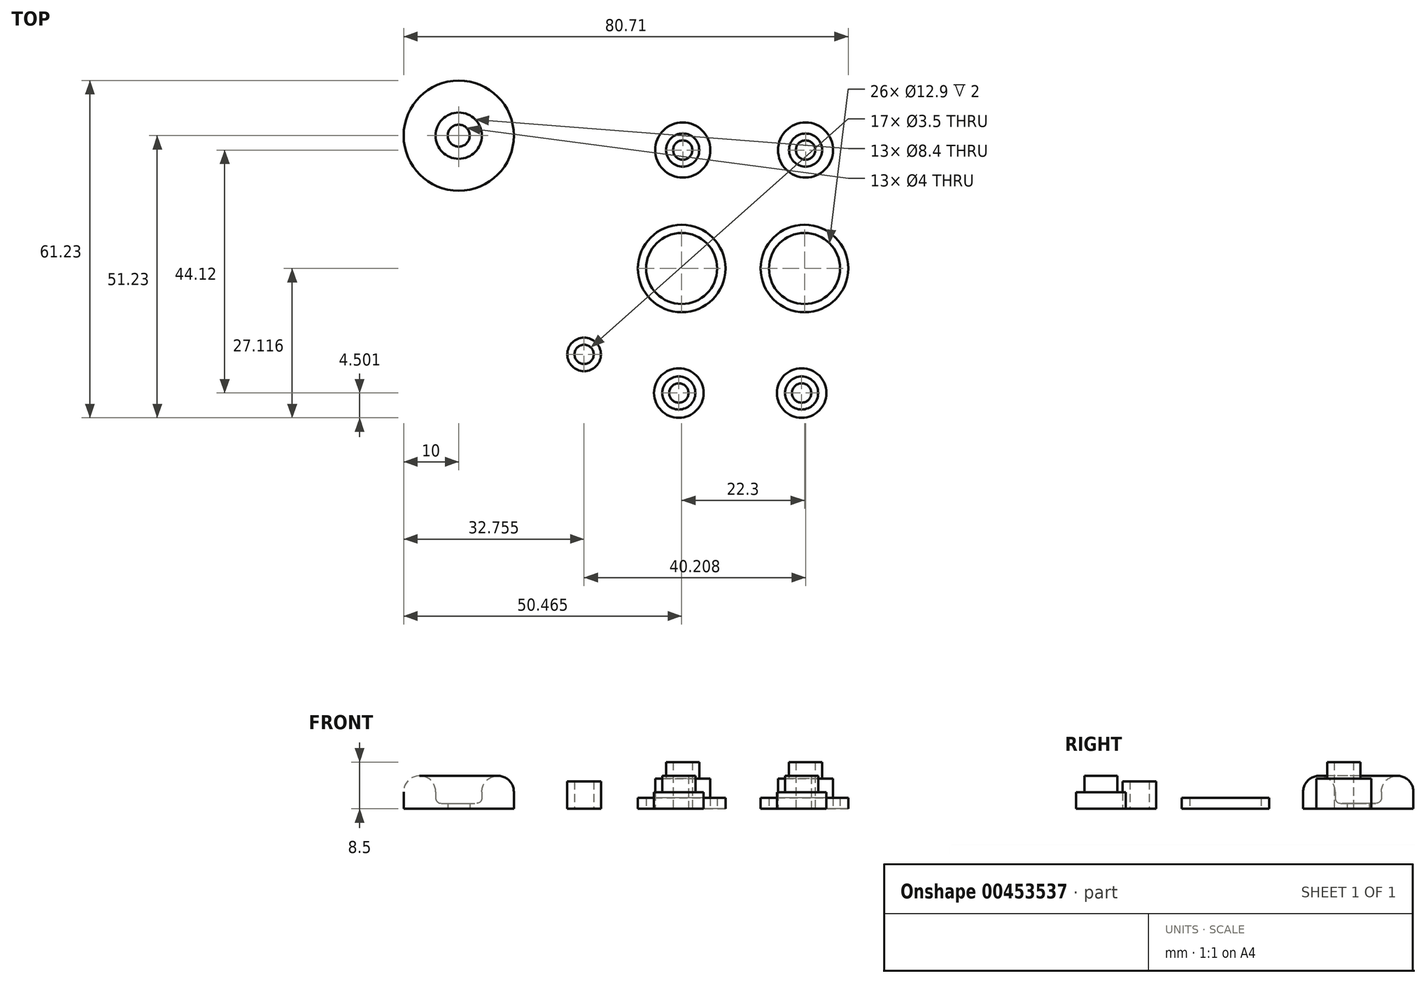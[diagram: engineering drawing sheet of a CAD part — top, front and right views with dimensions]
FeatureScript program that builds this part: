
annotation { "Feature Type Name" : "Feature", "Feature Type Description" : "" }
export const myFeature = defineFeature(function(context is Context, id is Id, definition is map)
    precondition{}
    {
        {
            var Q0;
            Q0=qCreatedBy(makeId("Front.planeOp"),FACE);
            var sketch = newSketch(context, id + "F0", { "sketchPlane" : qUnion([Q0])});
            skLineSegment(sketch, "E0.bottom", {"start": v(2, 0) * mm, "end": v(10, 0) * mm});
            skLineSegment(sketch, "E0.top", {"start": v(2, 1) * mm, "end": v(10, 1) * mm});
            skLineSegment(sketch, "E0.left", {"start": v(2, 0) * mm, "end": v(2, 1) * mm});
            skLineSegment(sketch, "E0.right", {"start": v(10, 0) * mm, "end": v(10, 1) * mm});
            skLineSegment(sketch, "E1", {"start": v(10, 1) * mm, "end": v(10, 3.1) * mm});
            skLineSegment(sketch, "E2", {"start": v(4.2, 1) * mm, "end": v(4.2, 3.1) * mm});
            skArc(sketch, "E3", {"start": v(10, 3.1) * mm, "mid": v(7.1, 6) * mm, "end": v(4.2, 3.1) * mm});
            skLineSegment(sketch, "E4", {"start": v(0, 0) * mm, "end": v(0, 11.31) * mm, "construction": true});
            skLineSegment(sketch, "E5", {"start": v(2.94, 6) * mm, "end": v(12.96, 6) * mm, "construction": true});
            skLineSegment(sketch, "E6", {"start": v(4.2, 3.1) * mm, "end": v(10, 3.1) * mm, "construction": true});
            skSolve(sketch);
        }
        {
            var Q0;
            Q0 = qSketchRegion(id + "F0", true);
            var Q1;
            Q1=sQuery(id+"F0.wireOp",EDGE,"E4");
            revolve(context, id + "F1", {"entities" : qUnion([Q0]), "axis" : qUnion([Q1]), "revolveType" : RevolveType.FULL});
        }
        {
            var Q0;
            Q0=makeQuery(id+"F1.opRevolve","SWEPT_EDGE",EDGE,{"disambiguationData":[OSD([sQuery(id+"F0.wireOp",EDGE,"E0.top"),sQuery(id+"F0.wireOp",EDGE,"E2")])]});
            fillet(context, id + "F2", {"entities" : qUnion([Q0]), "radius" : 1 * mm, "tangentPropagation" : true, "allowEdgeOverflow" : false});
        }
        {
            var Q0;
            Q0=qCreatedBy(makeId("Top.planeOp"),FACE);
            var sketch = newSketch(context, id + "F3", { "sketchPlane" : qUnion([Q0])});
            skCircle(sketch, "E7", {"center": v(22.75, -39.71) * mm, "radius": 1.75 * mm});
            skCircle(sketch, "E8", {"center": v(22.75, -39.71) * mm, "radius": 3.05 * mm});
            skSolve(sketch);
        }
        {
            var Q0;
            Q0 = qSketchRegion(id + "F3", true);
            extrude(context, id + "F4", {"entities" : qUnion([Q0]), "depth" : 5 * mm});
        }
        {
            var Q0;
            Q0=qCreatedBy(makeId("Top.planeOp"),FACE);
            var sketch = newSketch(context, id + "F5", { "sketchPlane" : qUnion([Q0])});
            skCircle(sketch, "E9", {"center": v(39.95, -46.73) * mm, "radius": 1.75 * mm});
            skCircle(sketch, "E10", {"center": v(39.95, -46.73) * mm, "radius": 4.5 * mm});
            skSolve(sketch);
        }
        {
            var Q0;
            Q0 = qSketchRegion(id + "F5", true);
            extrude(context, id + "F6", {"entities" : qUnion([Q0]), "depth" : 3 * mm});
        }
        {
            var Q0;
            Q0=makeQuery(id+"F6.opExtrude","CAP_FACE",FACE,{"disambiguationData":[OSD([sQuery(id+"F5.wireOp",EDGE,"E9"),sQuery(id+"F5.wireOp",EDGE,"E10")])],"isStart":false});
            var sketch = newSketch(context, id + "F7", { "sketchPlane" : qUnion([Q0])});
            skCircle(sketch, "E11", {"center": v(39.95, -46.73) * mm, "radius": 1.75 * mm});
            skCircle(sketch, "E12", {"center": v(39.95, -46.73) * mm, "radius": 3 * mm});
            skSolve(sketch);
        }
        {
            var Q0;
            Q0 = qSketchRegion(id + "F7", true);
            extrude(context, id + "F8", {"entities" : qUnion([Q0]), "operationType" : NewBodyOperationType.ADD, "depth" : 3 * mm});
        }
        {
            var Q0;
            Q0=qCreatedBy(makeId("Top.planeOp"),FACE);
            var sketch = newSketch(context, id + "F9", { "sketchPlane" : qUnion([Q0])});
            skCircle(sketch, "E13", {"center": v(40.46, -24.11) * mm, "radius": 7.95 * mm});
            skCircle(sketch, "E14", {"center": v(40.46, -24.11) * mm, "radius": 6.45 * mm});
            skSolve(sketch);
        }
        {
            var Q0;
            Q0 = qSketchRegion(id + "F9", true);
            extrude(context, id + "F10", {"entities" : qUnion([Q0]), "depth" : 2 * mm});
        }
        {
            var Q0;
            Q0=qCreatedBy(makeId("Top.planeOp"),FACE);
            var sketch = newSketch(context, id + "F11", { "sketchPlane" : qUnion([Q0])});
            skCircle(sketch, "E15", {"center": v(40.66, -2.6) * mm, "radius": 1.75 * mm});
            skCircle(sketch, "E16", {"center": v(40.66, -2.6) * mm, "radius": 5 * mm});
            skSolve(sketch);
        }
        {
            var Q0;
            Q0 = qSketchRegion(id + "F11", true);
            extrude(context, id + "F12", {"entities" : qUnion([Q0]), "depth" : 5.5 * mm});
        }
        {
            var Q0;
            Q0=makeQuery(id+"F12.opExtrude","CAP_FACE",FACE,{"disambiguationData":[OSD([sQuery(id+"F11.wireOp",EDGE,"E15"),sQuery(id+"F11.wireOp",EDGE,"E16")])],"isStart":false});
            var sketch = newSketch(context, id + "F13", { "sketchPlane" : qUnion([Q0])});
            skCircle(sketch, "E17", {"center": v(40.66, -2.6) * mm, "radius": 1.75 * mm});
            skCircle(sketch, "E18", {"center": v(40.66, -2.6) * mm, "radius": 3 * mm});
            skSolve(sketch);
        }
        {
            var Q0;
            Q0 = qSketchRegion(id + "F13", true);
            extrude(context, id + "F14", {"entities" : qUnion([Q0]), "operationType" : NewBodyOperationType.ADD, "depth" : 3 * mm});
        }
        {
            var Q0;
            Q0=makeQuery(id+"F6.opExtrude","SWEPT_BODY",BODY,{"disambiguationData":[OSD([sQuery(id+"F5.wireOp",EDGE,"E9"),sQuery(id+"F5.wireOp",EDGE,"E10")])]});
            var Q1;
            Q1=makeQuery(id+"F10.opExtrude","SWEPT_BODY",BODY,{"disambiguationData":[OSD([sQuery(id+"F9.wireOp",EDGE,"E13"),sQuery(id+"F9.wireOp",EDGE,"E14")])]});
            var Q2;
            Q2=makeQuery(id+"F12.opExtrude","SWEPT_BODY",BODY,{"disambiguationData":[OSD([sQuery(id+"F11.wireOp",EDGE,"E15"),sQuery(id+"F11.wireOp",EDGE,"E16")])]});
            var Q3;
            Q3=qCreatedBy(makeId("Right.planeOp"),FACE);
            transform(context, id + "F15", {"entities" : qUnion([Q0, Q1, Q2]), "transformType" : TransformType.TRANSLATION_DISTANCE, "transformDirection" : qUnion([Q3]), "distance" : 22.3 * mm, "makeCopy" : true});
        }
    });
